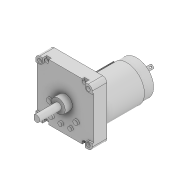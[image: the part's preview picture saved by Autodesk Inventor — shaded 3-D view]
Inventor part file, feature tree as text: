
AUTODESK INVENTOR PART (.ipt)
format: ipt  version: 2021 (Build 250183000, 183)  size: 454,144 bytes
history: native  units: mm
features: sketch x15, extrude x12, revolve x2, fillet x1, hole x1, plane x1
ambient origin geometry x8: Origin, YZ Plane, XZ Plane, XY Plane, X Axis, Y Axis, Z Axis, Center Point
bodies: Solid1 (feature_tree)
feature tree (32):
  extrude  "Extrusion1"  Depth=18.0mm TaperAngle=0.0deg
  fillet  "Fillet1"  Radius=5.0mm
  extrude  "Extrusion2"  Depth=5.0mm
  hole  "Hole1"  [1 undecoded]
  extrude  "Extrusion3"  Depth=5.7mm
  extrude  "Extrusion4"  Depth=3.0mm TaperAngle=0.0deg
  extrude  "Extrusion5"  Depth=9.0mm TaperAngle=0.0deg
  extrude  "Extrusion6"  Depth=7.0mm
  extrude  "Extrusion7"  Depth=27.0mm
  extrude  "Extrusion8"  Depth=16.0mm
  revolve  "Revolution1"  [1 undecoded]
  plane  "Work Plane1"
  extrude  "Extrusion9"  Depth=5.2mm
  revolve  "Revolution2"  [1 undecoded]
  extrude  "Extrusion10"  Depth=10.5mm
  extrude  "Extrusion11"  Depth=8.5mm
  extrude  "Extrusion12"  Depth=21.0mm
  sketch  "Sketch1"  dims[d0=70.0mm d2=18.0mm d3=0.0mm d4=5.0mm]
  sketch  "Sketch2"  dims[d5=5.0mm d6=5.0mm]
  sketch  "Sketch3"  dims[d7=5.0mm d9=1.2mm]
  sketch  "Sketch4"  dims[d10=2.0mm d11=0.0mm]
  sketch  "Sketch5"  dims[d12=3.9mm d13=6.0mm d14=5.0mm d15=7.2mm d16=9.690068mm d17=20.0mm d18=0.0mm d19=5.7mm]
  sketch  "Sketch6"  dims[d21=5.0mm d22=3.0mm d23=0.0mm]
  sketch  "Sketch7"  dims[d24=17.0mm d25=9.0mm d26=0.0mm]
  sketch  "Sketch8"  dims[d27=8.0mm d28=7.0mm]
  sketch  "Sketch9"  dims[d29=27.0mm d30=0.0mm d31=6.2mm]
  sketch  "Sketch10"  dims[d32=16.0mm d33=27.5mm]
  sketch  "Sketch11"  dims[d34=6.0mm d35=18.0mm]
  sketch  "Sketch12"  dims[d36=11.5mm d37=5.2mm]
  sketch  "Sketch13"  dims[d38=9.5mm d39=30.0mm]
  sketch  "Sketch14"  dims[d40=5.0mm d41=10.5mm]
  sketch  "Sketch15"  dims[d42=28.0mm d43=6.0mm d44=21.0mm d45=20.5mm d46=2.0mm d47=0.0mm d48=34.5mm d49=5.0mm d50=6.0mm d51=45.0deg d52=18.5mm d53=37.0mm d54=48.5mm d55=24.0mm d56=9.0mm d57=28.0mm d58=5.5mm d59=0.0mm d60=42.0mm d61=66.5mm d62=0.0mm d63=5.0mm d64=5.0mm d65=5.0mm d66=90.0deg d67=44.4mm d68=10.995574mm d69=45.0deg d70=49.0mm d71=0.0mm d72=3.0mm d73=2.0mm d74=2.5mm d75=7.5mm d76=1.0mm d77=1.0mm d78=6.5mm d79=2.0mm d80=1.5mm d82=90.0deg d83=8.726646mm d84=3.0mm d85=0.55mm d86=4.8mm d87=8.5mm d88=0.0mm d89=1.5mm d90=0.5mm d91=0.5mm d92=1.0mm d93=3.0mm d95=1.9mm d96=2.9mm d97=8.5mm d98=0.0mm d99=1.5mm d100=0.5mm d101=0.5mm d102=1.0mm d103=3.0mm d104=1.9mm d105=2.9mm d106=8.5mm d107=0.0mm]
note: 3 required parameter values undecoded (feature->parameter linkage not recoverable at this tier; creation-order binding heuristic only, values carry confidence <= 0.55)